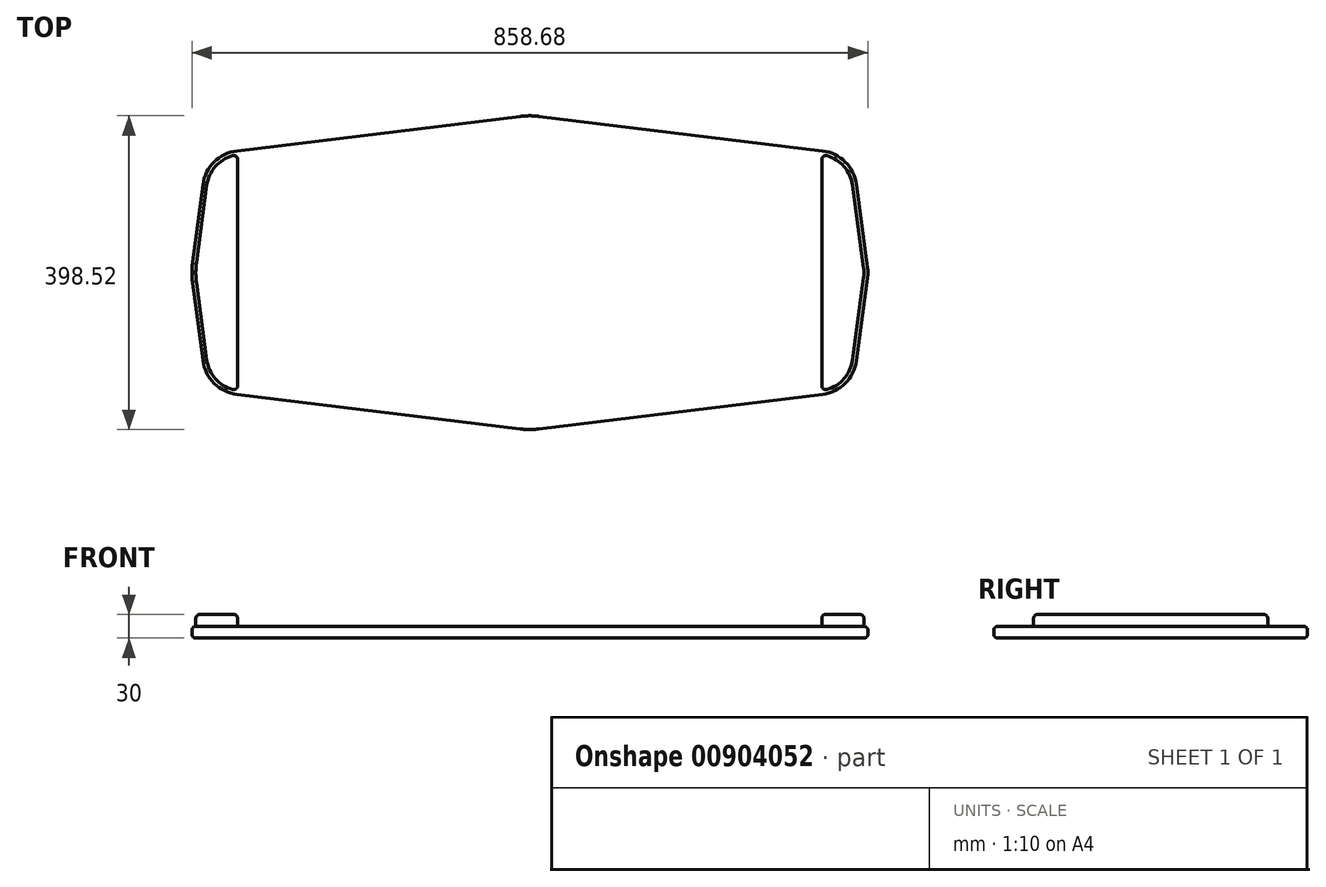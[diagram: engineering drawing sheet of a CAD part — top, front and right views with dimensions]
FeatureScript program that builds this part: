
annotation { "Feature Type Name" : "Feature", "Feature Type Description" : "" }
export const myFeature = defineFeature(function(context is Context, id is Id, definition is map)
    precondition{}
    {
        {
            var Q0;
            Q0=qCreatedBy(makeId("Top.planeOp"),FACE);
            var sketch = newSketch(context, id + "F0", { "sketchPlane" : qUnion([Q0])});
            skLineSegment(sketch, "E0", {"start": v(0, 0) * mm, "end": v(-430, 0) * mm, "construction": true});
            skLineSegment(sketch, "E1", {"start": v(-430, 0) * mm, "end": v(0, 0) * mm, "construction": true});
            skLineSegment(sketch, "E2", {"start": v(430, 0) * mm, "end": v(0, 0) * mm, "construction": true});
            skLineSegment(sketch, "E3", {"start": v(0, 200) * mm, "end": v(0, 0) * mm, "construction": true});
            skLineSegment(sketch, "E4", {"start": v(0, -200) * mm, "end": v(0, 0) * mm, "construction": true});
            skLineSegment(sketch, "E5", {"start": v(-410, 150) * mm, "end": v(-410, -150) * mm, "construction": true});
            skLineSegment(sketch, "E6", {"start": v(410, 150) * mm, "end": v(410, -150) * mm, "construction": true});
            skLineSegment(sketch, "E7", {"start": v(-428.24, 13.22) * mm, "end": v(-415.11, 111.66) * mm});
            skLineSegment(sketch, "E8", {"start": v(-428.24, -13.22) * mm, "end": v(-415.11, -111.66) * mm});
            skLineSegment(sketch, "E9", {"start": v(415.11, -111.66) * mm, "end": v(429.12, -6.6) * mm});
            skLineSegment(sketch, "E10", {"start": v(415.11, 111.66) * mm, "end": v(429.12, 6.6) * mm});
            skLineSegment(sketch, "E11", {"start": v(-371.6, 154.68) * mm, "end": v(-12.1, 198.52) * mm});
            skLineSegment(sketch, "E12", {"start": v(12.1, 198.52) * mm, "end": v(371.6, 154.68) * mm});
            skLineSegment(sketch, "E13", {"start": v(-371.6, -154.68) * mm, "end": v(-12.1, -198.52) * mm});
            skLineSegment(sketch, "E14", {"start": v(12.1, -198.52) * mm, "end": v(371.6, -154.68) * mm});
            skPoint(sketch, "E15.visualSharp", {"position": v(-410, 150) * mm});
            skArc(sketch, "E15.filletArc", {"start": v(-371.6, 154.68) * mm, "mid": v(-400.7, 140.6) * mm, "end": v(-415.11, 111.66) * mm});
            skPoint(sketch, "E16.visualSharp", {"position": v(-410, -150) * mm});
            skArc(sketch, "E16.filletArc", {"start": v(-415.11, -111.66) * mm, "mid": v(-400.7, -140.6) * mm, "end": v(-371.6, -154.68) * mm});
            skPoint(sketch, "E17.visualSharp", {"position": v(410, 150) * mm});
            skArc(sketch, "E17.filletArc", {"start": v(415.11, 111.66) * mm, "mid": v(400.7, 140.6) * mm, "end": v(371.6, 154.68) * mm});
            skPoint(sketch, "E18.visualSharp", {"position": v(410, -150) * mm});
            skArc(sketch, "E18.filletArc", {"start": v(371.6, -154.68) * mm, "mid": v(400.7, -140.6) * mm, "end": v(415.11, -111.66) * mm});
            skPoint(sketch, "E19.visualSharp", {"position": v(-430, 0) * mm});
            skArc(sketch, "E19.filletArc", {"start": v(-428.24, 13.22) * mm, "mid": v(-429.12, 0) * mm, "end": v(-428.24, -13.22) * mm});
            skPoint(sketch, "E20.visualSharp", {"position": v(430, 0) * mm});
            skArc(sketch, "E20.filletArc", {"start": v(429.12, -6.6) * mm, "mid": v(429.56, 0) * mm, "end": v(429.12, 6.6) * mm});
            skPoint(sketch, "E21.visualSharp", {"position": v(0, 200) * mm});
            skArc(sketch, "E21.filletArc", {"start": v(12.1, 198.52) * mm, "mid": v(0, 199.26) * mm, "end": v(-12.1, 198.52) * mm});
            skPoint(sketch, "E22.visualSharp", {"position": v(0, -200) * mm});
            skArc(sketch, "E22.filletArc", {"start": v(-12.1, -198.52) * mm, "mid": v(0, -199.26) * mm, "end": v(12.1, -198.52) * mm});
            skSolve(sketch);
        }
        {
            var Q0;
            Q0=makeQuery(id+"F0.imprint","IMPRINT",FACE,{"disambiguationData":[TD([[makeQuery(id+"F0.imprint","IMPRINT",EDGE,{"derivedFrom":sQuery(id+"F0.wireOp",EDGE,"E7")}),-1.0]])]});
            extrude(context, id + "F1", {"entities" : qUnion([Q0]), "depth" : 15 * mm, "offsetDistance" : 25 * mm});
        }
        {
            var Q0;
            Q0=makeQuery(id+"F1.opExtrude","CAP_FACE",FACE,{"disambiguationData":[OSD([sQuery(id+"F0.wireOp",EDGE,"E7"),sQuery(id+"F0.wireOp",EDGE,"E8"),sQuery(id+"F0.wireOp",EDGE,"E9"),sQuery(id+"F0.wireOp",EDGE,"E10"),sQuery(id+"F0.wireOp",EDGE,"E11"),sQuery(id+"F0.wireOp",EDGE,"E12"),sQuery(id+"F0.wireOp",EDGE,"E13"),sQuery(id+"F0.wireOp",EDGE,"E14"),sQuery(id+"F0.wireOp",EDGE,"E15.filletArc"),sQuery(id+"F0.wireOp",EDGE,"E16.filletArc"),sQuery(id+"F0.wireOp",EDGE,"E17.filletArc"),sQuery(id+"F0.wireOp",EDGE,"E18.filletArc"),sQuery(id+"F0.wireOp",EDGE,"E19.filletArc"),sQuery(id+"F0.wireOp",EDGE,"E20.filletArc"),sQuery(id+"F0.wireOp",EDGE,"E21.filletArc"),sQuery(id+"F0.wireOp",EDGE,"E22.filletArc")])],"isStart":false});
            fillet(context, id + "F2", {"entities" : qUnion([Q0]), "radius" : 5 * mm, "tangentPropagation" : true, "allowEdgeOverflow" : false});
        }
        {
            var Q0;
            Q0=makeQuery(id+"F1.opExtrude","CAP_FACE",FACE,{"disambiguationData":[OSD([sQuery(id+"F0.wireOp",EDGE,"E7"),sQuery(id+"F0.wireOp",EDGE,"E8"),sQuery(id+"F0.wireOp",EDGE,"E9"),sQuery(id+"F0.wireOp",EDGE,"E10"),sQuery(id+"F0.wireOp",EDGE,"E11"),sQuery(id+"F0.wireOp",EDGE,"E12"),sQuery(id+"F0.wireOp",EDGE,"E13"),sQuery(id+"F0.wireOp",EDGE,"E14"),sQuery(id+"F0.wireOp",EDGE,"E15.filletArc"),sQuery(id+"F0.wireOp",EDGE,"E16.filletArc"),sQuery(id+"F0.wireOp",EDGE,"E17.filletArc"),sQuery(id+"F0.wireOp",EDGE,"E18.filletArc"),sQuery(id+"F0.wireOp",EDGE,"E19.filletArc"),sQuery(id+"F0.wireOp",EDGE,"E20.filletArc"),sQuery(id+"F0.wireOp",EDGE,"E21.filletArc"),sQuery(id+"F0.wireOp",EDGE,"E22.filletArc")])],"isStart":true});
            fillet(context, id + "F3", {"entities" : qUnion([Q0]), "radius" : 5 * mm, "tangentPropagation" : true, "allowEdgeOverflow" : false});
        }
        {
            var Q0;
            Q0=makeQuery(id+"F1.opExtrude","CAP_FACE",FACE,{"disambiguationData":[OSD([sQuery(id+"F0.wireOp",EDGE,"E7"),sQuery(id+"F0.wireOp",EDGE,"E8"),sQuery(id+"F0.wireOp",EDGE,"E9"),sQuery(id+"F0.wireOp",EDGE,"E10"),sQuery(id+"F0.wireOp",EDGE,"E11"),sQuery(id+"F0.wireOp",EDGE,"E12"),sQuery(id+"F0.wireOp",EDGE,"E13"),sQuery(id+"F0.wireOp",EDGE,"E14"),sQuery(id+"F0.wireOp",EDGE,"E15.filletArc"),sQuery(id+"F0.wireOp",EDGE,"E16.filletArc"),sQuery(id+"F0.wireOp",EDGE,"E17.filletArc"),sQuery(id+"F0.wireOp",EDGE,"E18.filletArc"),sQuery(id+"F0.wireOp",EDGE,"E19.filletArc"),sQuery(id+"F0.wireOp",EDGE,"E20.filletArc"),sQuery(id+"F0.wireOp",EDGE,"E21.filletArc"),sQuery(id+"F0.wireOp",EDGE,"E22.filletArc")])],"isStart":false});
            var sketch = newSketch(context, id + "F4", { "sketchPlane" : qUnion([Q0])});
            skLineSegment(sketch, "E23.0.0", {"start": v(-371, -149.72) * mm, "end": v(-11.5, -193.56) * mm});
            skArc(sketch, "E23.0.1", {"start": v(-11.5, -193.56) * mm, "mid": v(0, -194.26) * mm, "end": v(11.5, -193.56) * mm});
            skLineSegment(sketch, "E23.0.2", {"start": v(11.5, -193.56) * mm, "end": v(371, -149.72) * mm});
            skArc(sketch, "E23.0.3", {"start": v(371, -149.72) * mm, "mid": v(397.2, -137.05) * mm, "end": v(410.16, -111) * mm});
            skLineSegment(sketch, "E23.0.4", {"start": v(410.16, -111) * mm, "end": v(424.16, -5.95) * mm});
            skArc(sketch, "E23.0.5", {"start": v(424.16, -5.95) * mm, "mid": v(424.56, 0) * mm, "end": v(424.16, 5.95) * mm});
            skLineSegment(sketch, "E23.0.6", {"start": v(424.16, 5.95) * mm, "end": v(410.16, 111) * mm});
            skArc(sketch, "E23.0.7", {"start": v(410.16, 111) * mm, "mid": v(397.2, 137.05) * mm, "end": v(371, 149.72) * mm});
            skLineSegment(sketch, "E23.0.8", {"start": v(371, 149.72) * mm, "end": v(11.5, 193.56) * mm});
            skArc(sketch, "E23.0.9", {"start": v(11.5, 193.56) * mm, "mid": v(0, 194.26) * mm, "end": v(-11.5, 193.56) * mm});
            skLineSegment(sketch, "E23.0.10", {"start": v(-11.5, 193.56) * mm, "end": v(-371, 149.72) * mm});
            skArc(sketch, "E23.0.11", {"start": v(-371, 149.72) * mm, "mid": v(-397.2, 137.05) * mm, "end": v(-410.16, 111) * mm});
            skLineSegment(sketch, "E23.0.12", {"start": v(-410.16, 111) * mm, "end": v(-423.28, 12.56) * mm});
            skArc(sketch, "E23.0.13", {"start": v(-423.28, 12.56) * mm, "mid": v(-424.12, 0) * mm, "end": v(-423.28, -12.56) * mm});
            skLineSegment(sketch, "E23.0.14", {"start": v(-423.28, -12.56) * mm, "end": v(-410.16, -111) * mm});
            skArc(sketch, "E23.0.15", {"start": v(-410.16, -111) * mm, "mid": v(-397.2, -137.05) * mm, "end": v(-371, -149.72) * mm});
            skLineSegment(sketch, "E24", {"start": v(371, -149.72) * mm, "end": v(371, 149.72) * mm});
            skLineSegment(sketch, "E25", {"start": v(-371, -149.72) * mm, "end": v(-371, 149.72) * mm});
            skSolve(sketch);
        }
        {
            var Q0;
            Q0=makeQuery(id+"F4.imprint","IMPRINT",FACE,{"disambiguationData":[TD([[makeQuery(id+"F4.imprint","IMPRINT",EDGE,{"derivedFrom":sQuery(id+"F4.wireOp",EDGE,"E23.0.3")}),1.0]])]});
            var Q1;
            Q1=makeQuery(id+"F4.imprint","IMPRINT",FACE,{"disambiguationData":[TD([[makeQuery(id+"F4.imprint","IMPRINT",EDGE,{"derivedFrom":sQuery(id+"F4.wireOp",EDGE,"E23.0.11")}),1.0]])]});
            extrude(context, id + "F5", {"entities" : qUnion([Q0, Q1]), "operationType" : NewBodyOperationType.ADD, "depth" : 15 * mm, "offsetDistance" : 25 * mm});
        }
        {
            var Q0;
            Q0=makeQuery(id+"F5.opExtrude","CAP_FACE",FACE,{"disambiguationData":[OSD([sQuery(id+"F4.wireOp",EDGE,"E23.0.11"),sQuery(id+"F4.wireOp",EDGE,"E23.0.12"),sQuery(id+"F4.wireOp",EDGE,"E23.0.13"),sQuery(id+"F4.wireOp",EDGE,"E23.0.14"),sQuery(id+"F4.wireOp",EDGE,"E23.0.15"),sQuery(id+"F4.wireOp",EDGE,"E25")])],"isStart":false});
            fillet(context, id + "F6", {"entities" : qUnion([Q0]), "radius" : 5 * mm, "tangentPropagation" : true, "allowEdgeOverflow" : false});
        }
        {
            var Q0;
            Q0=makeQuery(id+"F5.opExtrude","CAP_FACE",FACE,{"disambiguationData":[OSD([sQuery(id+"F4.wireOp",EDGE,"E23.0.3"),sQuery(id+"F4.wireOp",EDGE,"E23.0.4"),sQuery(id+"F4.wireOp",EDGE,"E23.0.5"),sQuery(id+"F4.wireOp",EDGE,"E23.0.6"),sQuery(id+"F4.wireOp",EDGE,"E23.0.7"),sQuery(id+"F4.wireOp",EDGE,"E24")])],"isStart":false});
            fillet(context, id + "F7", {"entities" : qUnion([Q0]), "radius" : 5 * mm, "tangentPropagation" : true, "allowEdgeOverflow" : false});
        }
        {
            var Q0;
            Q0=makeQuery(id+"F5.opExtrude","SWEPT_EDGE",EDGE,{"disambiguationData":[OSD([sQuery(id+"F4.wireOp",EDGE,"E23.0.0"),sQuery(id+"F4.wireOp",EDGE,"E23.0.15"),sQuery(id+"F4.wireOp",EDGE,"E25")])]});
            var Q1;
            Q1=makeQuery(id+"F5.opExtrude","SWEPT_EDGE",EDGE,{"disambiguationData":[OSD([sQuery(id+"F4.wireOp",EDGE,"E23.0.10"),sQuery(id+"F4.wireOp",EDGE,"E23.0.11"),sQuery(id+"F4.wireOp",EDGE,"E25")])]});
            var Q2;
            Q2=makeQuery(id+"F5.opExtrude","SWEPT_EDGE",EDGE,{"disambiguationData":[OSD([sQuery(id+"F4.wireOp",EDGE,"E23.0.2"),sQuery(id+"F4.wireOp",EDGE,"E23.0.3"),sQuery(id+"F4.wireOp",EDGE,"E24")])]});
            var Q3;
            Q3=makeQuery(id+"F5.opExtrude","SWEPT_EDGE",EDGE,{"disambiguationData":[OSD([sQuery(id+"F4.wireOp",EDGE,"E23.0.7"),sQuery(id+"F4.wireOp",EDGE,"E23.0.8"),sQuery(id+"F4.wireOp",EDGE,"E24")])]});
            fillet(context, id + "F8", {"entities" : qUnion([Q0, Q1, Q2, Q3]), "radius" : 5 * mm, "tangentPropagation" : true, "allowEdgeOverflow" : false});
        }
    });
